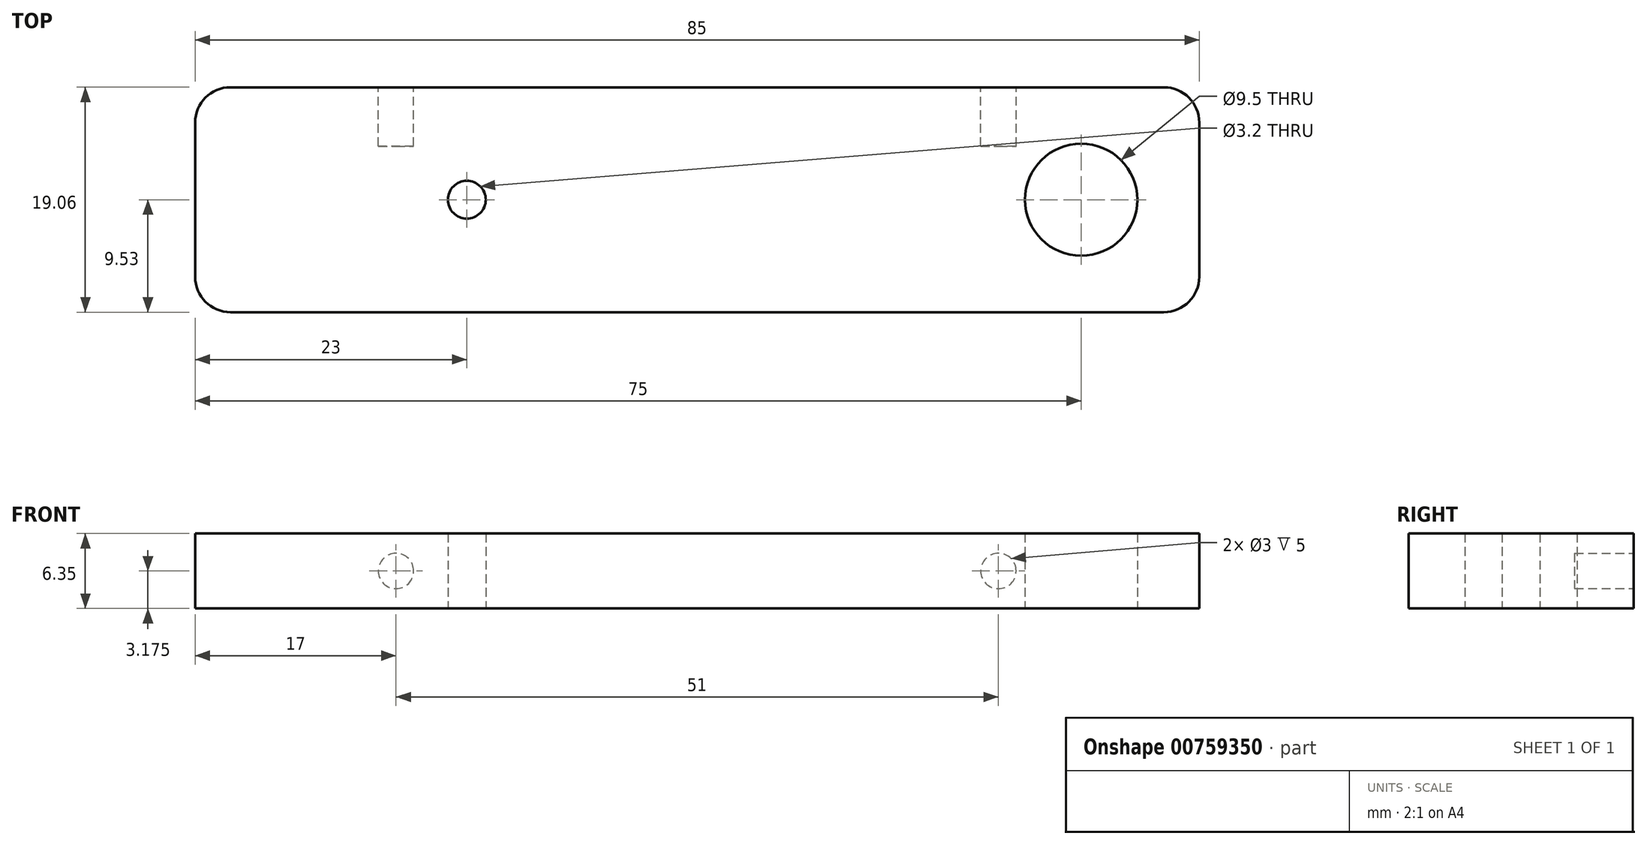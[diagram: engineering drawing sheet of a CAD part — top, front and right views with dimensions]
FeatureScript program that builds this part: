
annotation { "Feature Type Name" : "Feature", "Feature Type Description" : "" }
export const myFeature = defineFeature(function(context is Context, id is Id, definition is map)
    precondition{}
    {
        {
            var Q0;
            Q0=qCreatedBy(makeId("Top.planeOp"),FACE);
            var sketch = newSketch(context, id + "F0", { "sketchPlane" : qUnion([Q0])});
            skLineSegment(sketch, "E0.bottom", {"start": v(39.5, 9.52) * mm, "end": v(-39.5, 9.52) * mm});
            skLineSegment(sketch, "E0.top", {"start": v(39.5, -9.53) * mm, "end": v(-39.5, -9.53) * mm});
            skLineSegment(sketch, "E0.left", {"start": v(42.5, 6.53) * mm, "end": v(42.5, -6.53) * mm});
            skLineSegment(sketch, "E0.right", {"start": v(-42.5, 6.53) * mm, "end": v(-42.5, -6.53) * mm});
            skPoint(sketch, "E0.middle", {"position": v(0, 0) * mm});
            skPoint(sketch, "E1.visualSharp", {"position": v(-42.5, 9.52) * mm});
            skArc(sketch, "E1.filletArc", {"start": v(-39.5, 9.52) * mm, "mid": v(-41.62, 8.65) * mm, "end": v(-42.5, 6.53) * mm});
            skPoint(sketch, "E2.visualSharp", {"position": v(-42.5, -9.53) * mm});
            skArc(sketch, "E2.filletArc", {"start": v(-42.5, -6.53) * mm, "mid": v(-41.62, -8.65) * mm, "end": v(-39.5, -9.53) * mm});
            skPoint(sketch, "E3.visualSharp", {"position": v(42.5, -9.53) * mm});
            skArc(sketch, "E3.filletArc", {"start": v(39.5, -9.53) * mm, "mid": v(41.62, -8.65) * mm, "end": v(42.5, -6.53) * mm});
            skPoint(sketch, "E4.visualSharp", {"position": v(42.5, 9.52) * mm});
            skArc(sketch, "E4.filletArc", {"start": v(42.5, 6.53) * mm, "mid": v(41.62, 8.65) * mm, "end": v(39.5, 9.52) * mm});
            skCircle(sketch, "E5", {"center": v(32.5, 0) * mm, "radius": 4.75 * mm});
            skCircle(sketch, "E6", {"center": v(-19.5, 0) * mm, "radius": 1.6 * mm});
            skSolve(sketch);
        }
        {
            var Q0;
            Q0=makeQuery(id+"F0.imprint","IMPRINT",FACE,{"disambiguationData":[TD([[makeQuery(id+"F0.imprint","IMPRINT",EDGE,{"derivedFrom":sQuery(id+"F0.wireOp",EDGE,"E0.bottom")}),1.0]])]});
            extrude(context, id + "F1", {"entities" : qUnion([Q0]), "depth" : 6.35 * mm, "offsetDistance" : 25 * mm});
        }
        {
            var Q0;
            Q0=makeQuery(id+"F1.opExtrude","SWEPT_FACE",FACE,{"disambiguationData":[OSD([sQuery(id+"F0.wireOp",EDGE,"E0.bottom")])]});
            var sketch = newSketch(context, id + "F2", { "sketchPlane" : qUnion([Q0])});
            skCircle(sketch, "E7", {"center": v(-25.5, 3.18) * mm, "radius": 1.5 * mm});
            skPoint(sketch, "E7.centerSnap0", {"position": v(-39.5, 3.17) * mm});
            skCircle(sketch, "E8", {"center": v(25.5, 3.18) * mm, "radius": 1.5 * mm});
            skSolve(sketch);
        }
        {
            var Q0;
            Q0=makeQuery(id+"F2.imprint","IMPRINT",FACE,{"disambiguationData":[TD([[makeQuery(id+"F2.imprint","IMPRINT",EDGE,{"derivedFrom":sQuery(id+"F2.wireOp",EDGE,"E8")}),1.0]])]});
            var Q1;
            Q1=makeQuery(id+"F2.imprint","IMPRINT",FACE,{"disambiguationData":[TD([[makeQuery(id+"F2.imprint","IMPRINT",EDGE,{"derivedFrom":sQuery(id+"F2.wireOp",EDGE,"E7")}),1.0]])]});
            extrude(context, id + "F3", {"entities" : qUnion([Q0, Q1]), "operationType" : NewBodyOperationType.REMOVE, "oppositeDirection" : true, "depth" : 5 * mm, "offsetDistance" : 25 * mm});
        }
    });
